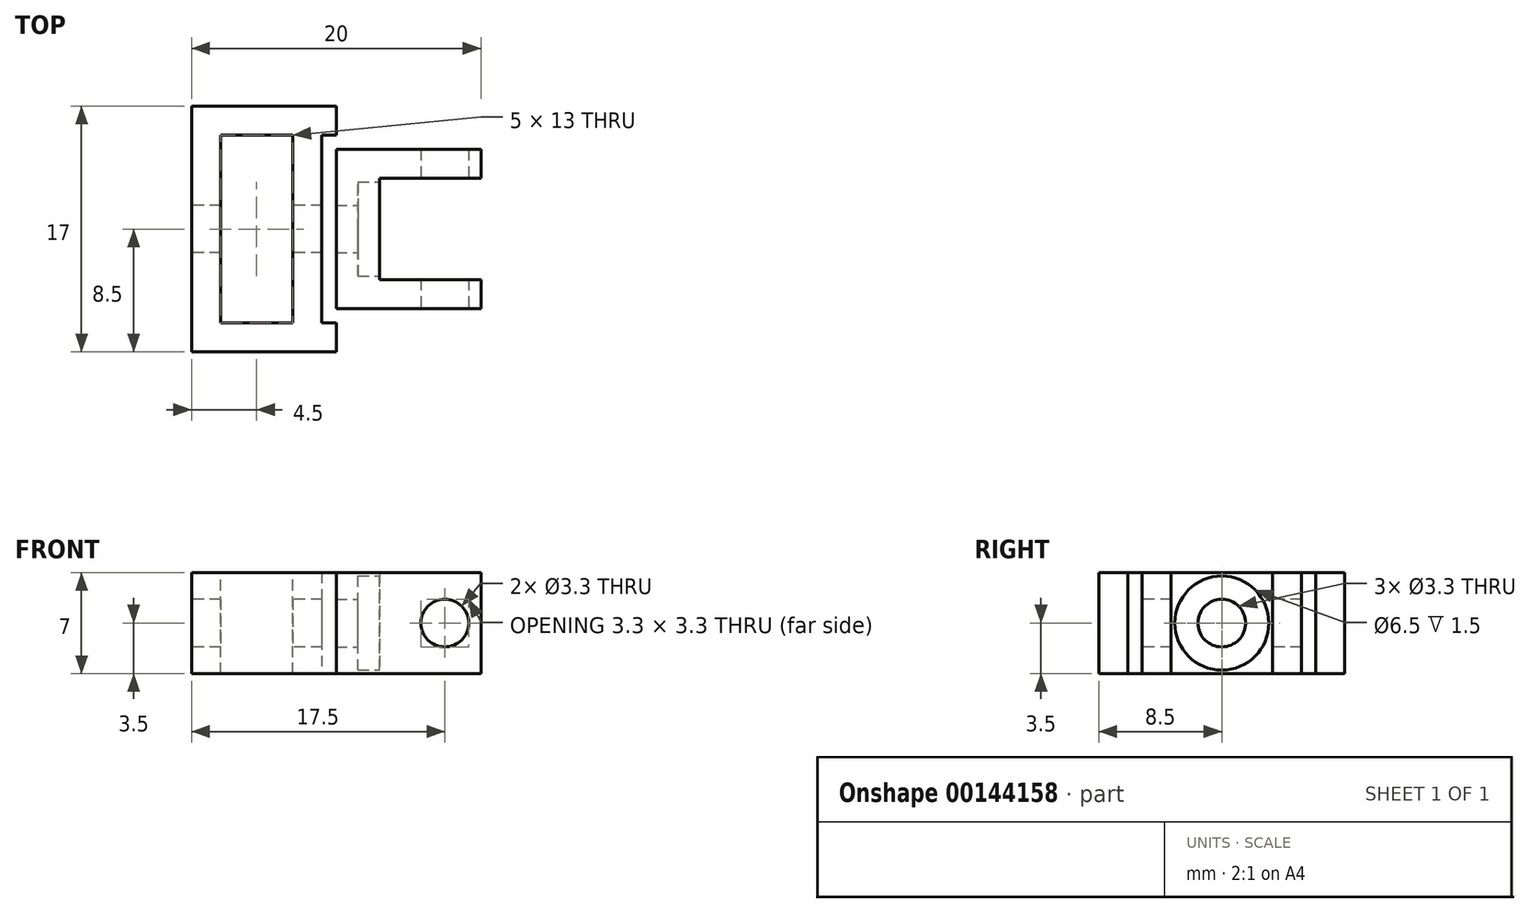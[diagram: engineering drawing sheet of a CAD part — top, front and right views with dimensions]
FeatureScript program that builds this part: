
annotation { "Feature Type Name" : "Feature", "Feature Type Description" : "" }
export const myFeature = defineFeature(function(context is Context, id is Id, definition is map)
    precondition{}
    {
        {
            var Q0;
            Q0=qCreatedBy(makeId("Top.planeOp"),FACE);
            var sketch = newSketch(context, id + "F0", { "sketchPlane" : qUnion([Q0])});
            skLineSegment(sketch, "E0", {"start": v(0, 0) * mm, "end": v(10, 0) * mm});
            skLineSegment(sketch, "E1", {"start": v(10, 0) * mm, "end": v(10, -2) * mm});
            skLineSegment(sketch, "E2", {"start": v(10, -2) * mm, "end": v(3, -2) * mm});
            skLineSegment(sketch, "E3", {"start": v(3, -2) * mm, "end": v(3, -9) * mm});
            skLineSegment(sketch, "E4", {"start": v(3, -9) * mm, "end": v(10, -9) * mm});
            skLineSegment(sketch, "E5", {"start": v(10, -9) * mm, "end": v(10, -11) * mm});
            skLineSegment(sketch, "E6", {"start": v(10, -11) * mm, "end": v(0, -11) * mm});
            skLineSegment(sketch, "E7", {"start": v(0, -11) * mm, "end": v(0, 0) * mm});
            skSolve(sketch);
        }
        {
            var Q0;
            Q0=makeQuery(id+"F0.imprint","IMPRINT",FACE,{"disambiguationData":[TD([[makeQuery(id+"F0.imprint","IMPRINT",EDGE,{"derivedFrom":sQuery(id+"F0.wireOp",EDGE,"E0")}),-1.0]])]});
            extrude(context, id + "F1", {"entities" : qUnion([Q0]), "depth" : 7 * mm});
        }
        {
            var Q0;
            Q0=makeQuery(id+"F1.opExtrude","SWEPT_FACE",FACE,{"disambiguationData":[OSD([sQuery(id+"F0.wireOp",EDGE,"E6")])]});
            var sketch = newSketch(context, id + "F2", { "sketchPlane" : qUnion([Q0])});
            skLineSegment(sketch, "E8", {"start": v(7.5, 7) * mm, "end": v(7.5, 3.5) * mm, "construction": true});
            skLineSegment(sketch, "E9", {"start": v(7.5, 3.5) * mm, "end": v(7.5, 0) * mm, "construction": true});
            skLineSegment(sketch, "E10", {"start": v(7.5, 3.5) * mm, "end": v(10, 3.5) * mm, "construction": true});
            skSolve(sketch);
        }
        {
            var Q0;
            Q0=sQuery(id+"F2.wireOp",VERTEX,"E10.start");
            var Q1;
            Q1=makeQuery(id+"F1.opExtrude","SWEPT_BODY",BODY,{"disambiguationData":[OSD([sQuery(id+"F0.wireOp",EDGE,"E0"),sQuery(id+"F0.wireOp",EDGE,"E1"),sQuery(id+"F0.wireOp",EDGE,"E2"),sQuery(id+"F0.wireOp",EDGE,"E3"),sQuery(id+"F0.wireOp",EDGE,"E4"),sQuery(id+"F0.wireOp",EDGE,"E5"),sQuery(id+"F0.wireOp",EDGE,"E6"),sQuery(id+"F0.wireOp",EDGE,"E7")])]});
            hole(context, id + "F3", {"style" : HoleStyle.SIMPLE, "endStyle" : HoleEndStyle.THROUGH, "standardTappedOrClearance" : lookupTablePath({ "standard" : "ISO", "fit" : "Normal", "size" : "M3", "type" : "Clearance" }), "standardBlindInLast" : lookupTablePath({ "fit" : "Standard", "standard" : "ISO", "size" : "M3", "type" : "Clearance" }), "holeDiameter" : 3.3 * mm, "startFromSketch" : true, "locations" : qUnion([Q0]), "scope" : qUnion([Q1]), "isTappedThrough" : true});
        }
        {
            var Q0;
            Q0=makeQuery(id+"F1.opExtrude","SWEPT_FACE",FACE,{"disambiguationData":[OSD([sQuery(id+"F0.wireOp",EDGE,"E3")])]});
            var sketch = newSketch(context, id + "F4", { "sketchPlane" : qUnion([Q0])});
            skLineSegment(sketch, "E11", {"start": v(-9, 3.5) * mm, "end": v(-5.5, 3.5) * mm, "construction": true});
            skLineSegment(sketch, "E12", {"start": v(-5.5, 3.5) * mm, "end": v(-2, 3.5) * mm, "construction": true});
            skLineSegment(sketch, "E13", {"start": v(-5.5, 3.5) * mm, "end": v(-5.5, 7) * mm, "construction": true});
            skLineSegment(sketch, "E14", {"start": v(-5.5, 3.5) * mm, "end": v(-5.5, 0) * mm, "construction": true});
            skSolve(sketch);
        }
        {
            var Q0;
            Q0=sQuery(id+"F4.wireOp",VERTEX,"E11.end");
            var Q1;
            Q1=makeQuery(id+"F1.opExtrude","SWEPT_BODY",BODY,{"disambiguationData":[OSD([sQuery(id+"F0.wireOp",EDGE,"E0"),sQuery(id+"F0.wireOp",EDGE,"E1"),sQuery(id+"F0.wireOp",EDGE,"E2"),sQuery(id+"F0.wireOp",EDGE,"E3"),sQuery(id+"F0.wireOp",EDGE,"E4"),sQuery(id+"F0.wireOp",EDGE,"E5"),sQuery(id+"F0.wireOp",EDGE,"E6"),sQuery(id+"F0.wireOp",EDGE,"E7")])]});
            hole(context, id + "F5", {"style" : HoleStyle.C_BORE, "endStyle" : HoleEndStyle.THROUGH, "holeDiameter" : 3.3 * mm, "cBoreDiameter" : 6.5 * mm, "cBoreDepth" : 1.5 * mm, "locations" : qUnion([Q0]), "scope" : qUnion([Q1]), "isTappedThrough" : true});
        }
        {
            var Q0;
            Q0=qCreatedBy(makeId("Top.planeOp"),FACE);
            var sketch = newSketch(context, id + "F6", { "sketchPlane" : qUnion([Q0])});
            skLineSegment(sketch, "E15", {"start": v(0, 1) * mm, "end": v(0, 3) * mm});
            skLineSegment(sketch, "E16", {"start": v(0, 3) * mm, "end": v(-10, 3) * mm});
            skLineSegment(sketch, "E17", {"start": v(-10, 3) * mm, "end": v(-10, -14) * mm});
            skLineSegment(sketch, "E18", {"start": v(-10, -14) * mm, "end": v(0, -14) * mm});
            skLineSegment(sketch, "E19", {"start": v(0, -14) * mm, "end": v(0, -12) * mm});
            skLineSegment(sketch, "E20", {"start": v(0, -12) * mm, "end": v(-1, -12) * mm});
            skLineSegment(sketch, "E21", {"start": v(-1, -12) * mm, "end": v(-1, 1) * mm});
            skLineSegment(sketch, "E22", {"start": v(-1, 1) * mm, "end": v(0, 1) * mm});
            skSolve(sketch);
        }
        {
            var Q0;
            Q0=makeQuery(id+"F6.imprint","IMPRINT",FACE,{"disambiguationData":[TD([[makeQuery(id+"F6.imprint","IMPRINT",EDGE,{"derivedFrom":sQuery(id+"F6.wireOp",EDGE,"E15")}),1.0]])]});
            extrude(context, id + "F7", {"entities" : qUnion([Q0]), "depth" : 7 * mm});
        }
        {
            var Q0;
            Q0=makeQuery(id+"F7.opExtrude","CAP_FACE",FACE,{"disambiguationData":[OSD([sQuery(id+"F6.wireOp",EDGE,"E15"),sQuery(id+"F6.wireOp",EDGE,"E16"),sQuery(id+"F6.wireOp",EDGE,"E17"),sQuery(id+"F6.wireOp",EDGE,"E18"),sQuery(id+"F6.wireOp",EDGE,"E19"),sQuery(id+"F6.wireOp",EDGE,"E20"),sQuery(id+"F6.wireOp",EDGE,"E21"),sQuery(id+"F6.wireOp",EDGE,"E22")])],"isStart":false});
            var sketch = newSketch(context, id + "F8", { "sketchPlane" : qUnion([Q0])});
            skLineSegment(sketch, "E23.bottom", {"start": v(-8, 1) * mm, "end": v(-3, 1) * mm});
            skLineSegment(sketch, "E23.top", {"start": v(-8, -12) * mm, "end": v(-3, -12) * mm});
            skLineSegment(sketch, "E23.left", {"start": v(-8, 1) * mm, "end": v(-8, -12) * mm});
            skLineSegment(sketch, "E23.right", {"start": v(-3, 1) * mm, "end": v(-3, -12) * mm});
            skLineSegment(sketch, "E24", {"start": v(-8, 1) * mm, "end": v(-8, 3) * mm, "construction": true});
            skLineSegment(sketch, "E25", {"start": v(-8, -12) * mm, "end": v(-8, -14) * mm, "construction": true});
            skLineSegment(sketch, "E26", {"start": v(-8, -5.5) * mm, "end": v(-10, -5.5) * mm, "construction": true});
            skLineSegment(sketch, "E27", {"start": v(-3, -5.5) * mm, "end": v(-1, -5.5) * mm, "construction": true});
            skSolve(sketch);
        }
        {
            var Q0;
            Q0=makeQuery(id+"F8.imprint","IMPRINT",FACE,{"disambiguationData":[TD([[makeQuery(id+"F8.imprint","IMPRINT",EDGE,{"derivedFrom":sQuery(id+"F8.wireOp",EDGE,"E23.bottom")}),-1.0]])]});
            extrude(context, id + "F9", {"entities" : qUnion([Q0]), "operationType" : NewBodyOperationType.REMOVE, "endBound" : BoundingType.THROUGH_ALL, "oppositeDirection" : true, "depth" : 25 * mm});
        }
        {
            var Q0;
            Q0=makeQuery(id+"F7.opExtrude","SWEPT_FACE",FACE,{"disambiguationData":[OSD([sQuery(id+"F6.wireOp",EDGE,"E17")])]});
            var sketch = newSketch(context, id + "F10", { "sketchPlane" : qUnion([Q0])});
            skLineSegment(sketch, "E28", {"start": v(5.5, 7) * mm, "end": v(5.5, 3.5) * mm, "construction": true});
            skPoint(sketch, "E28.endSnap0", {"position": v(5.5, 7) * mm});
            skLineSegment(sketch, "E29", {"start": v(5.5, 3.5) * mm, "end": v(5.5, 0) * mm});
            skLineSegment(sketch, "E30", {"start": v(5.5, 0) * mm, "end": v(5.5, 3.5) * mm, "construction": true});
            skLineSegment(sketch, "E31", {"start": v(-3, 3.5) * mm, "end": v(5.5, 3.5) * mm, "construction": true});
            skLineSegment(sketch, "E32", {"start": v(5.5, 3.5) * mm, "end": v(14, 3.5) * mm, "construction": true});
            skSolve(sketch);
        }
        {
            var Q0;
            Q0=sQuery(id+"F10.wireOp",VERTEX,"E30.end");
            var Q1;
            Q1=makeQuery(id+"F7.opExtrude","SWEPT_BODY",BODY,{"disambiguationData":[OSD([sQuery(id+"F6.wireOp",EDGE,"E15"),sQuery(id+"F6.wireOp",EDGE,"E16"),sQuery(id+"F6.wireOp",EDGE,"E17"),sQuery(id+"F6.wireOp",EDGE,"E18"),sQuery(id+"F6.wireOp",EDGE,"E19"),sQuery(id+"F6.wireOp",EDGE,"E20"),sQuery(id+"F6.wireOp",EDGE,"E21"),sQuery(id+"F6.wireOp",EDGE,"E22")])]});
            hole(context, id + "F11", {"style" : HoleStyle.SIMPLE, "endStyle" : HoleEndStyle.THROUGH, "holeDiameter" : 3.3 * mm, "startFromSketch" : true, "locations" : qUnion([Q0]), "scope" : qUnion([Q1]), "isTappedThrough" : true});
        }
    });
